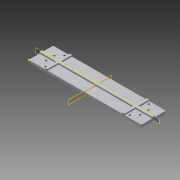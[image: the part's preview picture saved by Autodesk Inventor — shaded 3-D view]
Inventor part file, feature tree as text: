
AUTODESK INVENTOR PART (.ipt)
format: ipt  version: 2015 (Build 190159000, 159)  size: 174,080 bytes
history: native  units: mm
features: sketch x8, extrude x7, mirror x4, plane x2, fillet x1
ambient origin geometry x8: Origin, YZ Plane, XZ Plane, XY Plane, X Axis, Y Axis, Z Axis, Center Point
bodies: Solid1 (feature_tree)
feature tree (22):
  extrude  "Extrusion1"  Depth=51.0mm
  extrude  "Extrusion2"  Depth=6.0mm
  sketch  "Sketch3"  dims[d5=3.0mm d6=0.0mm d7=5.0mm]
  sketch  "Sketch5"  dims[d13=5.0mm d14=3.0mm d15=0.0mm]
  extrude  "Extrusion5"  Depth=5.0mm
  extrude  "Extrusion6"  Depth=3.0mm TaperAngle=0.0deg
  extrude  "Extrusion7"  Depth=3.0mm TaperAngle=0.0deg
  extrude  "Extrusion9"  Depth=3.2mm
  sketch  "Sketch9"  dims[d24=3.2mm d25=3.2mm]
  plane  "Work Plane1"
  mirror  "Mirror1"
  plane  "Work Plane2"
  mirror  "Mirror2"
  extrude  "Extrusion10"  Depth=5.0mm
  mirror  "Mirror3"
  mirror  "Mirror4"
  fillet  "Fillet1"  Radius=15.0mm
  sketch  "Sketch12"  dims[d30=16.875mm d31=10.0mm d32=0.0mm d33=90.0deg d34=90.0deg d35=4.2mm d36=4.2mm d37=10.0mm d38=0.0mm d39=2.0mm]
  sketch  "Sketch1"  dims[d0=235.0mm d1=51.0mm]
  sketch  "Sketch2"  dims[d2=5.0mm d3=0.0mm d4=6.0mm]
  sketch  "Sketch8"  dims[d16=3.0mm d17=0.0mm d18=3.0mm d19=0.0mm]
  sketch  "Sketch11"  dims[d27=5.0mm d28=5.625mm d29=15.0mm]
